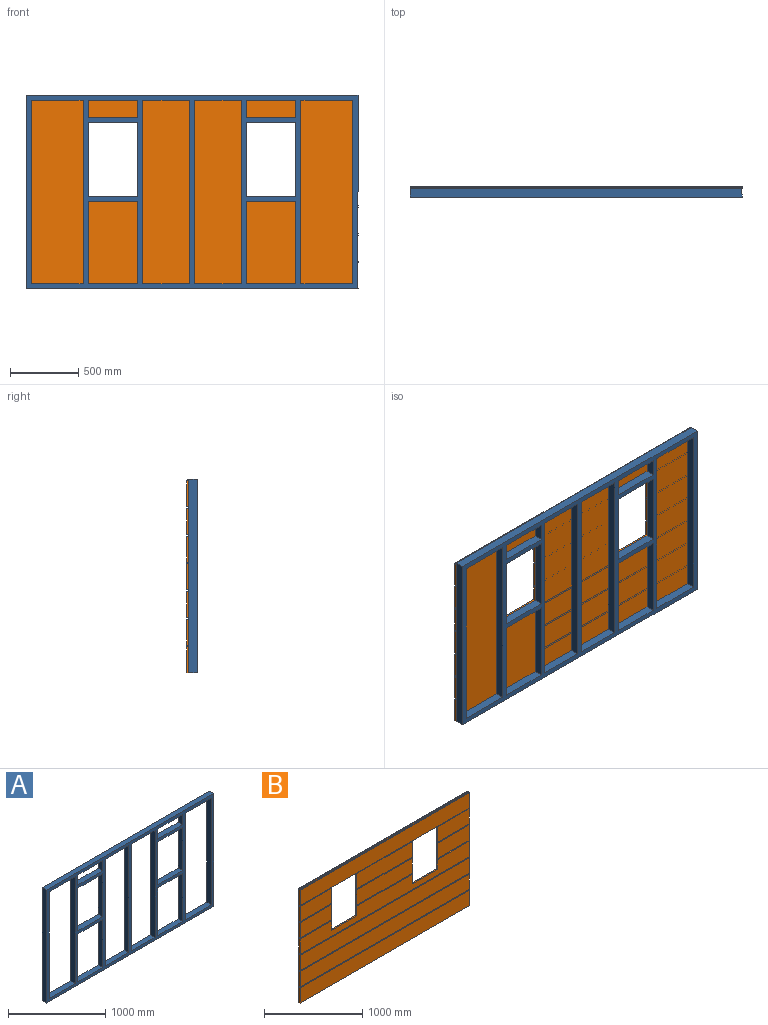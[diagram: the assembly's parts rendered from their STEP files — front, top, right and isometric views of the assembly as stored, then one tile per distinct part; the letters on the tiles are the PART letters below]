
ASSEMBLY  parts=2 mates=3
PART A: 46 faces, bbox 2438.4x63.5x1422.4 mm
  f0: plane 539.75x63.5mm, normal (-1,0,0), area 34274.1mm2, adj f1,f43,f44,f45
  f1: plane 361.95x63.5mm, normal (0,0,1), area 22983.8mm2, adj f0,f2,f44,f45
  f2: plane 539.75x63.5mm, normal (1,0,0), area 34274.1mm2, adj f1,f43,f44,f45
  f3: plane 342.9x63.5mm, normal (0,0,-1), area 21774.2mm2, adj f4,f33,f44,f45
  f4: plane 1346.2x63.5mm, normal (-1,0,0), area 85483.7mm2, adj f3,f5,f44,f45
  f5: plane 342.9x63.5mm, normal (0,0,1), area 21774.2mm2, adj f4,f33,f44,f45
  f6: plane 127x63.5mm, normal (1,0,0), area 8064.5mm2, adj f7,f34,f44,f45
  f7: plane 361.95x63.5mm, normal (0,0,-1), area 22983.8mm2, adj f6,f8,f44,f45
  f8: plane 127x63.5mm, normal (-1,0,0), area 8064.5mm2, adj f7,f34,f44,f45
  f9: plane 381x63.5mm, normal (0,0,-1), area 24193.5mm2, adj f10,f35,f44,f45
  f10: plane 1346.2x63.5mm, normal (-1,0,0), area 85483.7mm2, adj f9,f11,f44,f45
  f11: plane 381x63.5mm, normal (0,0,1), area 24193.5mm2, adj f10,f35,f44,f45
  f12: plane 127x63.5mm, normal (1,0,0), area 8064.5mm2, adj f13,f36,f44,f45
  f13: plane 361.95x63.5mm, normal (0,0,-1), area 22983.8mm2, adj f12,f14,f44,f45
  f14: plane 127x63.5mm, normal (-1,0,0), area 8064.5mm2, adj f13,f36,f44,f45
  f15: plane 342.9x63.5mm, normal (0,0,1), area 21774.1mm2, adj f16,f37,f44,f45
  f16: plane 1346.2x63.5mm, normal (1,0,0), area 85483.7mm2, adj f15,f17,f44,f45
  f17: plane 342.9x63.5mm, normal (0,0,-1), area 21774.1mm2, adj f16,f37,f44,f45
  f18: plane 1422.4x63.5mm, normal (1,0,0), area 90322.4mm2, adj f19,f38,f44,f45
  f19: plane 2438.4x63.5mm, normal (0,0,1), area 154838.4mm2, adj f18,f20,f44,f45
  f20: plane 1422.4x63.5mm, normal (-1,0,0), area 90322.4mm2, adj f19,f38,f44,f45
  f21: plane 361.95x63.5mm, normal (0,0,1), area 22983.8mm2, adj f22,f39,f44,f45
  f22: plane 603.25x63.5mm, normal (1,0,0), area 38306.4mm2, adj f21,f23,f44,f45
  f23: plane 361.95x63.5mm, normal (0,0,-1), area 22983.8mm2, adj f22,f39,f44,f45
  f24: plane 539.75x63.5mm, normal (-1,0,0), area 34274.1mm2, adj f25,f40,f44,f45
  f25: plane 361.95x63.5mm, normal (0,0,1), area 22983.8mm2, adj f24,f26,f44,f45
  f26: plane 539.75x63.5mm, normal (1,0,0), area 34274.1mm2, adj f25,f40,f44,f45
  f27: plane 381x63.5mm, normal (0,0,1), area 24193.5mm2, adj f28,f41,f44,f45
  f28: plane 1346.2x63.5mm, normal (1,0,0), area 85483.7mm2, adj f27,f29,f44,f45
  f29: plane 381x63.5mm, normal (0,0,-1), area 24193.5mm2, adj f28,f41,f44,f45
  f30: plane 361.95x63.5mm, normal (0,0,1), area 22983.8mm2, adj f31,f42,f44,f45
  f31: plane 603.25x63.5mm, normal (1,0,0), area 38306.4mm2, adj f30,f32,f44,f45
  f32: plane 361.95x63.5mm, normal (0,0,-1), area 22983.8mm2, adj f31,f42,f44,f45
  f33: plane 1346.2x63.5mm, normal (1,0,0), area 85483.7mm2, adj f3,f5,f44,f45
  f34: plane 361.95x63.5mm, normal (0,0,1), area 22983.8mm2, adj f6,f8,f44,f45
  f35: plane 1346.2x63.5mm, normal (1,0,0), area 85483.7mm2, adj f9,f11,f44,f45
  f36: plane 361.95x63.5mm, normal (0,0,1), area 22983.8mm2, adj f12,f14,f44,f45
  f37: plane 1346.2x63.5mm, normal (-1,0,0), area 85483.7mm2, adj f15,f17,f44,f45
  f38: plane 2438.4x63.5mm, normal (0,0,-1), area 154838.4mm2, adj f18,f20,f44,f45
  f39: plane 603.25x63.5mm, normal (-1,0,0), area 38306.4mm2, adj f21,f23,f44,f45
  f40: plane 361.95x63.5mm, normal (0,0,-1), area 22983.8mm2, adj f24,f26,f44,f45
  f41: plane 1346.2x63.5mm, normal (-1,0,0), area 85483.7mm2, adj f27,f29,f44,f45
  f42: plane 603.25x63.5mm, normal (-1,0,0), area 38306.4mm2, adj f30,f32,f44,f45
  f43: plane 361.95x63.5mm, normal (0,0,-1), area 22983.8mm2, adj f0,f2,f44,f45
  f44: plane 2438.4x1422.4mm, normal (0,-1,0), area 599998.8mm2, adj f0,f1,f2,f3,f4,f5,f6,f7
  f45: plane 2438.4x1422.4mm, normal (0,1,0), area 599998.8mm2, adj f0,f1,f2,f3,f4,f5,f6,f7
PART B: 58 faces, bbox 2438.4x14.7x1422.4 mm
  f0: plane 1422.4x14.68mm, normal (1,0,0), area 20092.2mm2, adj f2,f3,f6,f9,f10,f11,f12,f15
  f1: plane 1422.4x14.68mm, normal (-1,0,0), area 20092.2mm2, adj f2,f3,f4,f7,f10,f11,f12,f15
  f2: plane 2438.4x5.79mm, normal (0,0,1), area 14121.3mm2, adj f0,f1,f22,f57
  f3: plane 2438.4x190.5mm, normal (0,-1,0), area 464515.2mm2, adj f0,f1,f15,f56
  f4: plane 457.2x190.5mm, normal (0,-1,0), area 87096.6mm2, adj f1,f17,f48,f54
  f5: plane 800.1x190.5mm, normal (0,-1,0), area 152419mm2, adj f14,f19,f42,f51
  f6: plane 457.2x190.5mm, normal (0,-1,0), area 87096.6mm2, adj f0,f18,f45,f53
  f7: plane 457.2x190.5mm, normal (0,-1,0), area 87096.6mm2, adj f1,f17,f39,f47
  f8: plane 800.1x190.5mm, normal (0,-1,0), area 152419.1mm2, adj f14,f19,f33,f43
  f9: plane 457.2x190.5mm, normal (0,-1,0), area 87096.6mm2, adj f0,f18,f36,f46
  f10: plane 2438.4x190.5mm, normal (0,-1,0), area 377176.7mm2, adj f0,f1,f13,f14,f16,f17,f18,f19
  f11: plane 2438.4x190.5mm, normal (0,-1,0), area 464515.2mm2, adj f0,f1,f27,f29
  f12: plane 2438.4x190.5mm, normal (0,-1,0), area 464515.2mm2, adj f0,f1,f24,f26
  f13: plane 361.95x14.68mm, normal (0,0,1), area 5313.9mm2, adj f10,f14,f18,f22
  f14: plane 539.75x14.68mm, normal (1,0,0), area 7585.5mm2, adj f5,f8,f10,f13,f15,f22,f32,f33
  f15: plane 2438.4x14.68mm, normal (0,0,-1), area 25869.6mm2, adj f0,f1,f3,f14,f17,f18,f19,f22
  f16: plane 361.95x14.68mm, normal (0,0,1), area 5313.9mm2, adj f10,f17,f19,f22
  f17: plane 539.75x14.68mm, normal (1,0,0), area 7585.5mm2, adj f4,f7,f10,f15,f16,f22,f38,f39
  f18: plane 539.75x14.68mm, normal (-1,0,0), area 7585.5mm2, adj f6,f9,f10,f13,f15,f22,f35,f36
  f19: plane 539.75x14.68mm, normal (-1,0,0), area 7585.5mm2, adj f5,f8,f10,f15,f16,f22,f32,f33
  f20: plane 2438.4x14.68mm, normal (0,0,-1), area 35798.6mm2, adj f0,f1,f21,f22
  f21: plane 2438.4x190.5mm, normal (0,-1,0), area 464515.2mm2, adj f0,f1,f20,f23
  f22: plane 2438.4x1422.4mm, normal (0,1,0), area 3077655.1mm2, adj f0,f1,f2,f13,f14,f15,f16,f17
  f23: plane 2438.4x8.89mm, normal (0,0,1), area 21677.4mm2, adj f0,f1,f21,f25
  f24: plane 2438.4x8.89mm, normal (0,0,-1), area 21677.4mm2, adj f0,f1,f12,f25
  f25: plane 2438.4x12.7mm, normal (0,-1,0), area 30967.7mm2, adj f0,f1,f23,f24
  f26: plane 2438.4x8.89mm, normal (0,0,1), area 21677.4mm2, adj f0,f1,f12,f28
  f27: plane 2438.4x8.89mm, normal (0,0,-1), area 21677.4mm2, adj f0,f1,f11,f28
  f28: plane 2438.4x12.7mm, normal (0,-1,0), area 30967.7mm2, adj f0,f1,f26,f27
  f29: plane 2438.4x8.89mm, normal (0,0,1), area 21677.4mm2, adj f0,f1,f11,f31
  f30: plane 2438.4x8.89mm, normal (0,0,-1), area 21677.4mm2, adj f0,f1,f10,f31
  f31: plane 2438.4x12.7mm, normal (0,-1,0), area 30967.7mm2, adj f0,f1,f29,f30
  f32: plane 800.1x12.7mm, normal (0,-1,0), area 10161.3mm2, adj f14,f19,f33,f34
  f33: plane 800.1x8.89mm, normal (0,0,-1), area 7112.9mm2, adj f8,f14,f19,f32
  f34: plane 800.1x8.89mm, normal (0,0,1), area 7112.9mm2, adj f10,f14,f19,f32
  f35: plane 457.2x12.7mm, normal (0,-1,0), area 5806.4mm2, adj f0,f18,f36,f37
  f36: plane 457.2x8.89mm, normal (0,0,-1), area 4064.5mm2, adj f0,f9,f18,f35
  f37: plane 457.2x8.89mm, normal (0,0,1), area 4064.5mm2, adj f0,f10,f18,f35
  f38: plane 457.2x8.89mm, normal (0,0,1), area 4064.5mm2, adj f1,f10,f17,f40
  f39: plane 457.2x8.89mm, normal (0,0,-1), area 4064.5mm2, adj f1,f7,f17,f40
  f40: plane 457.2x12.7mm, normal (0,-1,0), area 5806.4mm2, adj f1,f17,f38,f39
  f41: plane 800.1x12.7mm, normal (0,-1,0), area 10161.3mm2, adj f14,f19,f42,f43
  f42: plane 800.1x8.89mm, normal (0,0,-1), area 7112.9mm2, adj f5,f14,f19,f41
  f43: plane 800.1x8.89mm, normal (0,0,1), area 7112.9mm2, adj f8,f14,f19,f41
  f44: plane 457.2x12.7mm, normal (0,-1,0), area 5806.4mm2, adj f0,f18,f45,f46
  f45: plane 457.2x8.89mm, normal (0,0,-1), area 4064.5mm2, adj f0,f6,f18,f44
  f46: plane 457.2x8.89mm, normal (0,0,1), area 4064.5mm2, adj f0,f9,f18,f44
  f47: plane 457.2x8.89mm, normal (0,0,1), area 4064.5mm2, adj f1,f7,f17,f49
  f48: plane 457.2x8.89mm, normal (0,0,-1), area 4064.5mm2, adj f1,f4,f17,f49
  f49: plane 457.2x12.7mm, normal (0,-1,0), area 5806.4mm2, adj f1,f17,f47,f48
  f50: plane 800.1x12.7mm, normal (0,-1,0), area 10161.3mm2, adj f14,f15,f19,f51
  f51: plane 800.1x8.89mm, normal (0,0,1), area 7112.9mm2, adj f5,f14,f19,f50
  f52: plane 457.2x12.7mm, normal (0,-1,0), area 5806.4mm2, adj f0,f15,f18,f53
  f53: plane 457.2x8.89mm, normal (0,0,1), area 4064.5mm2, adj f0,f6,f18,f52
  f54: plane 457.2x8.89mm, normal (0,0,1), area 4064.5mm2, adj f1,f4,f17,f55
  f55: plane 457.2x12.7mm, normal (0,-1,0), area 5806.4mm2, adj f1,f15,f17,f54
  f56: plane 2438.4x8.89mm, normal (0,0,1), area 21677.4mm2, adj f0,f1,f3,f57
  f57: plane 2438.4x12.7mm, normal (0,-1,0), area 30967.7mm2, adj f0,f1,f2,f56
PLACE A t=(0,2438.4,97.63)mm
PLACE B rot(axis=(0,0,-1),180deg) t=(2438.4,2438.4,97.63)mm
MATE planar A.f18 <-> B.f1  axis (1,0,0) through (2438.4,2406.65,808.83)mm
MATE planar A.f45 <-> B.f22  axis (0,1,0) through (1219.2,2438.4,830.72)mm
MATE planar A.f38 <-> B.f20  axis (0,0,-1) through (1219.2,2406.65,97.63)mm
